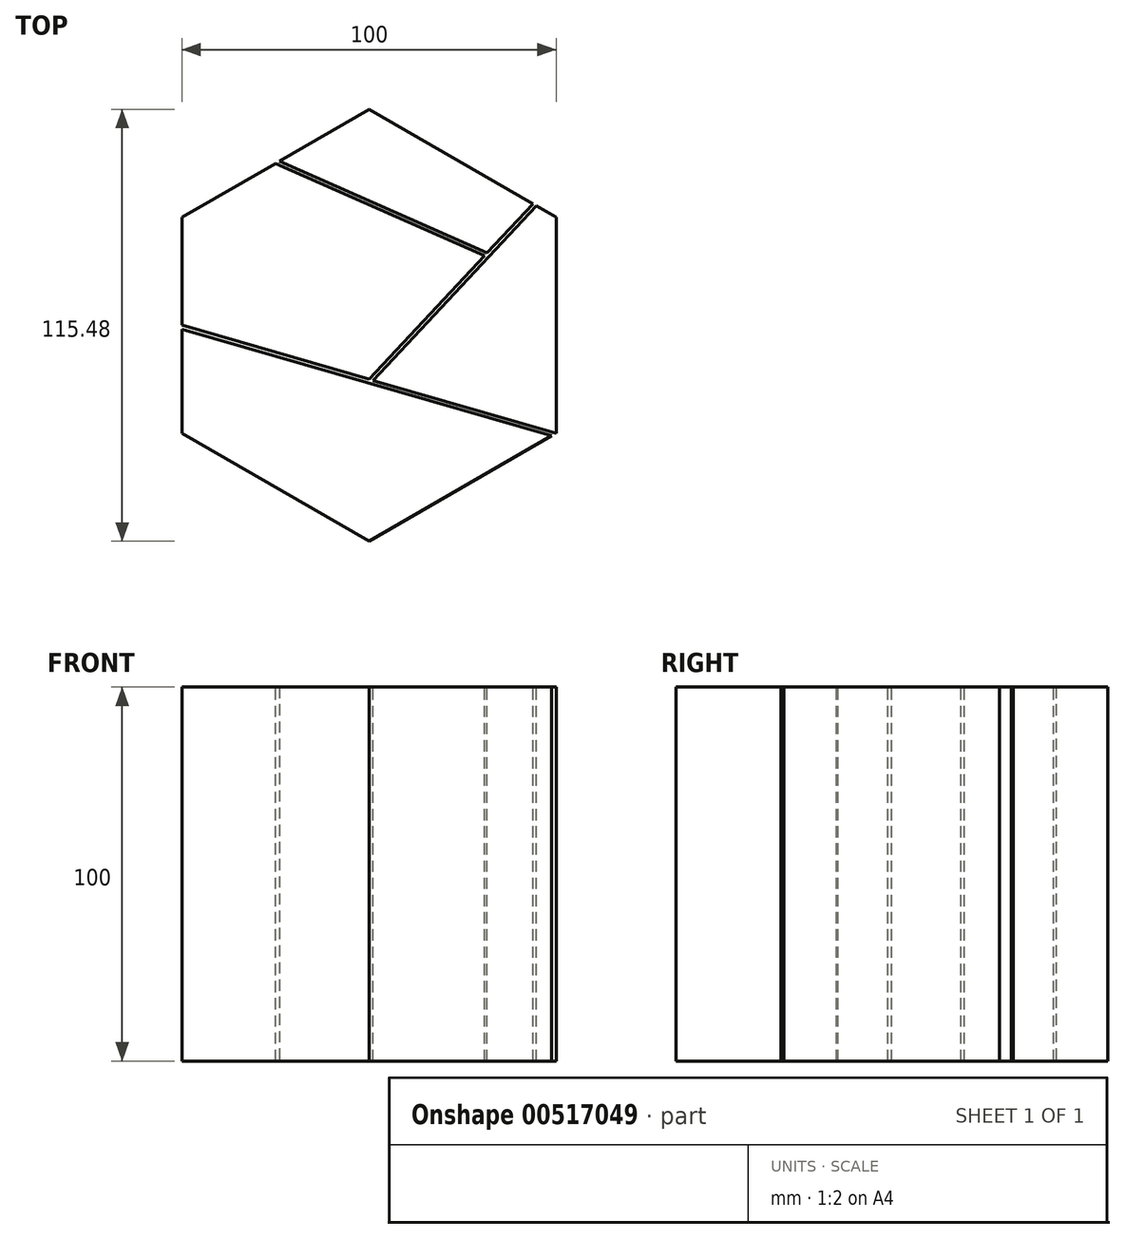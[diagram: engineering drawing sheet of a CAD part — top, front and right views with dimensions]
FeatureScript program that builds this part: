
annotation { "Feature Type Name" : "Feature", "Feature Type Description" : "" }
export const myFeature = defineFeature(function(context is Context, id is Id, definition is map)
    precondition{}
    {
        {
            var Q0;
            Q0=qCreatedBy(makeId("Top.planeOp"),FACE);
            var sketch = newSketch(context, id + "F0", { "sketchPlane" : qUnion([Q0])});
            skCircle(sketch, "E0.cCircle", {"center": v(0, 0) * mm, "radius": 50 * mm, "construction": true});
            skLineSegment(sketch, "E0.0", {"start": v(-50, -28.87) * mm, "end": v(-50, 28.87) * mm});
            skLineSegment(sketch, "E0.1", {"start": v(-50, 28.87) * mm, "end": v(0, 57.74) * mm});
            skLineSegment(sketch, "E0.2", {"start": v(0, 57.74) * mm, "end": v(50, 28.87) * mm});
            skLineSegment(sketch, "E0.3", {"start": v(50, 28.87) * mm, "end": v(50, -28.87) * mm});
            skLineSegment(sketch, "E0.4", {"start": v(50, -28.87) * mm, "end": v(0, -57.74) * mm});
            skLineSegment(sketch, "E0.5", {"start": v(0, -57.74) * mm, "end": v(-50, -28.87) * mm});
            skPoint(sketch, "E0.0.midPoint", {"position": v(-50, 0) * mm});
            skSolve(sketch);
        }
        {
            var Q0;
            Q0 = qSketchRegion(id + "F0", true);
            extrude(context, id + "F1", {"entities" : qUnion([Q0]), "depth" : 100 * mm, "offsetDistance" : 25 * mm});
        }
        {
            var Q0;
            Q0=makeQuery(id+"F1.opExtrude","CAP_FACE",FACE,{"disambiguationData":[OSD([sQuery(id+"F0.wireOp",EDGE,"E0.0"),sQuery(id+"F0.wireOp",EDGE,"E0.1"),sQuery(id+"F0.wireOp",EDGE,"E0.2"),sQuery(id+"F0.wireOp",EDGE,"E0.3"),sQuery(id+"F0.wireOp",EDGE,"E0.4"),sQuery(id+"F0.wireOp",EDGE,"E0.5")])],"isStart":false});
            var sketch = newSketch(context, id + "F2", { "sketchPlane" : qUnion([Q0])});
            skLineSegment(sketch, "E1", {"start": v(-50, 0) * mm, "end": v(50, -28.87) * mm});
            skLineSegment(sketch, "E2", {"start": v(-50, 0) * mm, "end": v(-50.28, -0.96) * mm});
            skLineSegment(sketch, "E3", {"start": v(-50.28, -0.96) * mm, "end": v(55.48, -31.5) * mm});
            skLineSegment(sketch, "E4", {"start": v(55.48, -31.5) * mm, "end": v(50, -28.87) * mm});
            skLineSegment(sketch, "E5", {"start": v(1.08, -14.74) * mm, "end": v(44.68, 31.94) * mm});
            skLineSegment(sketch, "E6", {"start": v(44.68, 31.94) * mm, "end": v(44.68, 33.4) * mm});
            skLineSegment(sketch, "E7", {"start": v(44.68, 33.4) * mm, "end": v(0, -14.43) * mm});
            skLineSegment(sketch, "E8", {"start": v(30.84, 18.58) * mm, "end": v(-25, 43.3) * mm});
            skLineSegment(sketch, "E9", {"start": v(31.56, 19.35) * mm, "end": v(-35, 48.82) * mm});
            skLineSegment(sketch, "E10", {"start": v(-35, 48.82) * mm, "end": v(-25, 43.3) * mm});
            skPoint(sketch, "E11", {"position": v(-25, 43.3) * mm});
            skSolve(sketch);
        }
        {
            var Q0;
            Q0 = qSketchRegion(id + "F2", true);
            extrude(context, id + "F3", {"entities" : qUnion([Q0]), "operationType" : NewBodyOperationType.REMOVE, "oppositeDirection" : true, "depth" : 110.7 * mm, "offsetDistance" : 25 * mm});
        }
    });
